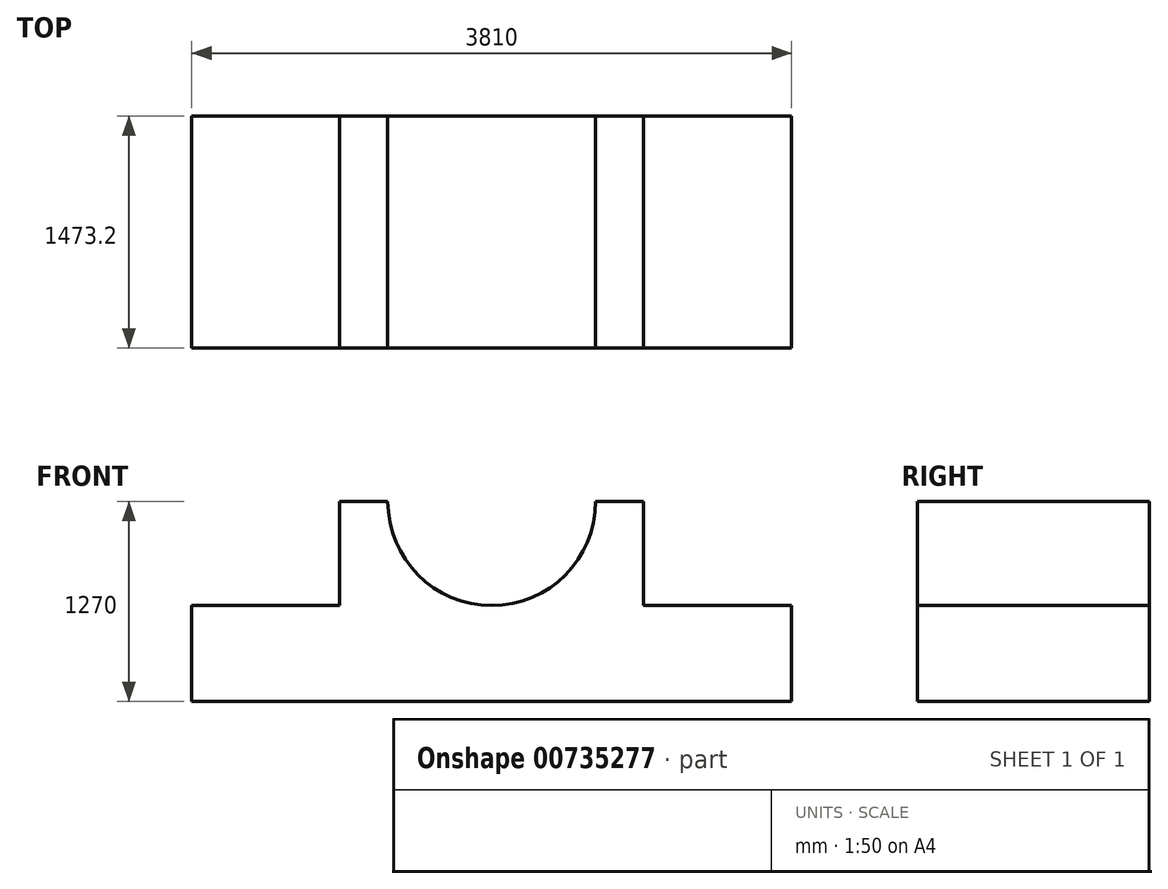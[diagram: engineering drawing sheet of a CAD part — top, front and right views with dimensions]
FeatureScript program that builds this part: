
annotation { "Feature Type Name" : "Feature", "Feature Type Description" : "" }
export const myFeature = defineFeature(function(context is Context, id is Id, definition is map)
    precondition{}
    {
        {
            var Q0;
            Q0=qCreatedBy(makeId("Front.planeOp"),FACE);
            var sketch = newSketch(context, id + "F0", { "sketchPlane" : qUnion([Q0])});
            skLineSegment(sketch, "E0", {"start": v(-73.61, -16.4) * mm, "end": v(3736.39, -16.4) * mm});
            skLineSegment(sketch, "E1", {"start": v(-73.61, -16.4) * mm, "end": v(-73.61, 593.2) * mm});
            skLineSegment(sketch, "E2", {"start": v(3736.39, -16.4) * mm, "end": v(3736.39, 593.2) * mm});
            skLineSegment(sketch, "E3", {"start": v(-73.61, 593.2) * mm, "end": v(866.19, 593.2) * mm});
            skLineSegment(sketch, "E4", {"start": v(3736.39, 593.2) * mm, "end": v(2796.59, 593.2) * mm});
            skLineSegment(sketch, "E5", {"start": v(2796.59, 593.2) * mm, "end": v(2796.59, 1253.6) * mm});
            skLineSegment(sketch, "E6", {"start": v(866.19, 593.2) * mm, "end": v(866.19, 1253.6) * mm});
            skLineSegment(sketch, "E7", {"start": v(866.19, 1253.6) * mm, "end": v(1170.99, 1253.6) * mm});
            skCircle(sketch, "E8", {"center": v(1831.39, 1253.6) * mm, "radius": 660.4 * mm});
            skLineSegment(sketch, "E9", {"start": v(2796.59, 1253.6) * mm, "end": v(2491.79, 1253.6) * mm});
            skSolve(sketch);
        }
        {
            var Q0;
            Q0=makeQuery(id+"F0.imprint","IMPRINT",FACE,{"disambiguationData":[TD([[makeQuery(id+"F0.imprint","IMPRINT",EDGE,{"derivedFrom":sQuery(id+"F0.wireOp",EDGE,"E0")}),1.0]])]});
            extrude(context, id + "F1", {"entities" : qUnion([Q0]), "depth" : 1473.2 * mm, "offsetDistance" : 25.4 * mm});
        }
    });
